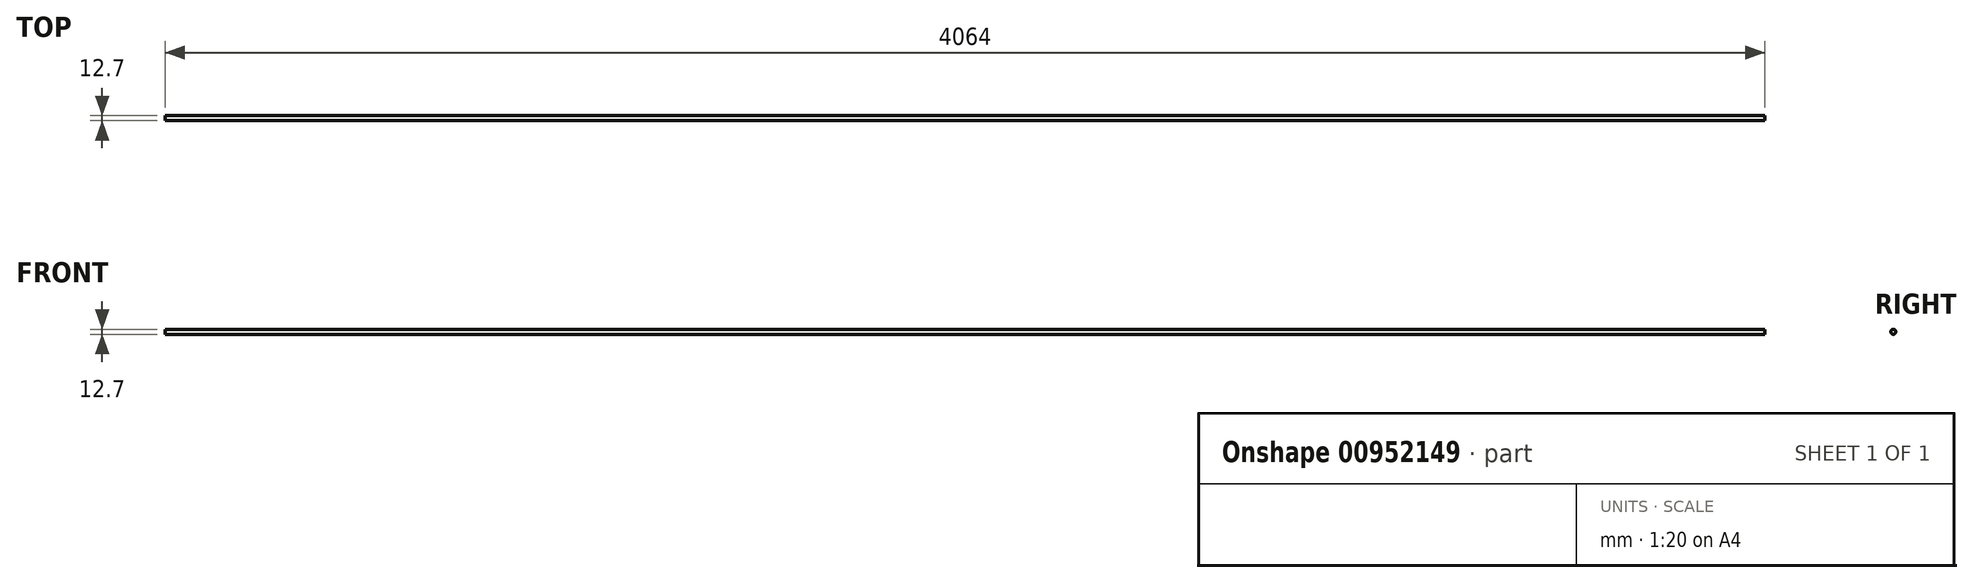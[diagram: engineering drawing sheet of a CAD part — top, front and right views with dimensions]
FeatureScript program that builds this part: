
annotation { "Feature Type Name" : "Feature", "Feature Type Description" : "" }
export const myFeature = defineFeature(function(context is Context, id is Id, definition is map)
    precondition{}
    {
        {
            var Q0;
            Q0=qCreatedBy(makeId("Right.planeOp"),FACE);
            var sketch = newSketch(context, id + "F0", { "sketchPlane" : qUnion([Q0])});
            skCircle(sketch, "E0", {"center": v(0, 0) * mm, "radius": 6.35 * mm});
            skSolve(sketch);
        }
        {
            var Q0;
            Q0=makeQuery(id+"F0.imprint","IMPRINT",FACE,{"disambiguationData":[TD([[makeQuery(id+"F0.imprint","IMPRINT",EDGE,{"derivedFrom":sQuery(id+"F0.wireOp",EDGE,"E0")}),1.0]])]});
            extrude(context, id + "F1", {"entities" : qUnion([Q0]), "depth" : 4064 * mm, "offsetDistance" : 25.4 * mm});
        }
    });
